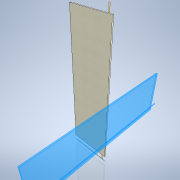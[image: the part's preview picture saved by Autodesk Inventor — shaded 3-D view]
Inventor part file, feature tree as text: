
AUTODESK INVENTOR PART (.ipt)
format: ipt  version: 2021 (Build 250183000, 183)  size: 103,424 bytes
history: native  units: mm
features: other x4, extrude x1, sketch x1, reference x1
ambient origin geometry x8: Origin, YZ Plane, XZ Plane, XY Plane, X Axis, Y Axis, Z Axis, Center Point
bodies: Body1 (feature_tree)
feature tree (7):
  other  "Bryła1"
  other  "Płaszczyzna konstrukcyjna1"
  extrude  "Wyciągnięcie proste1"  Depth=600.0mm
  sketch  "Szkic1"
  reference  "Odniesienie1"
  other  "Zespół1"
  other  "ISO 10799-2 - 25x25x2.5 - 2000:1"
